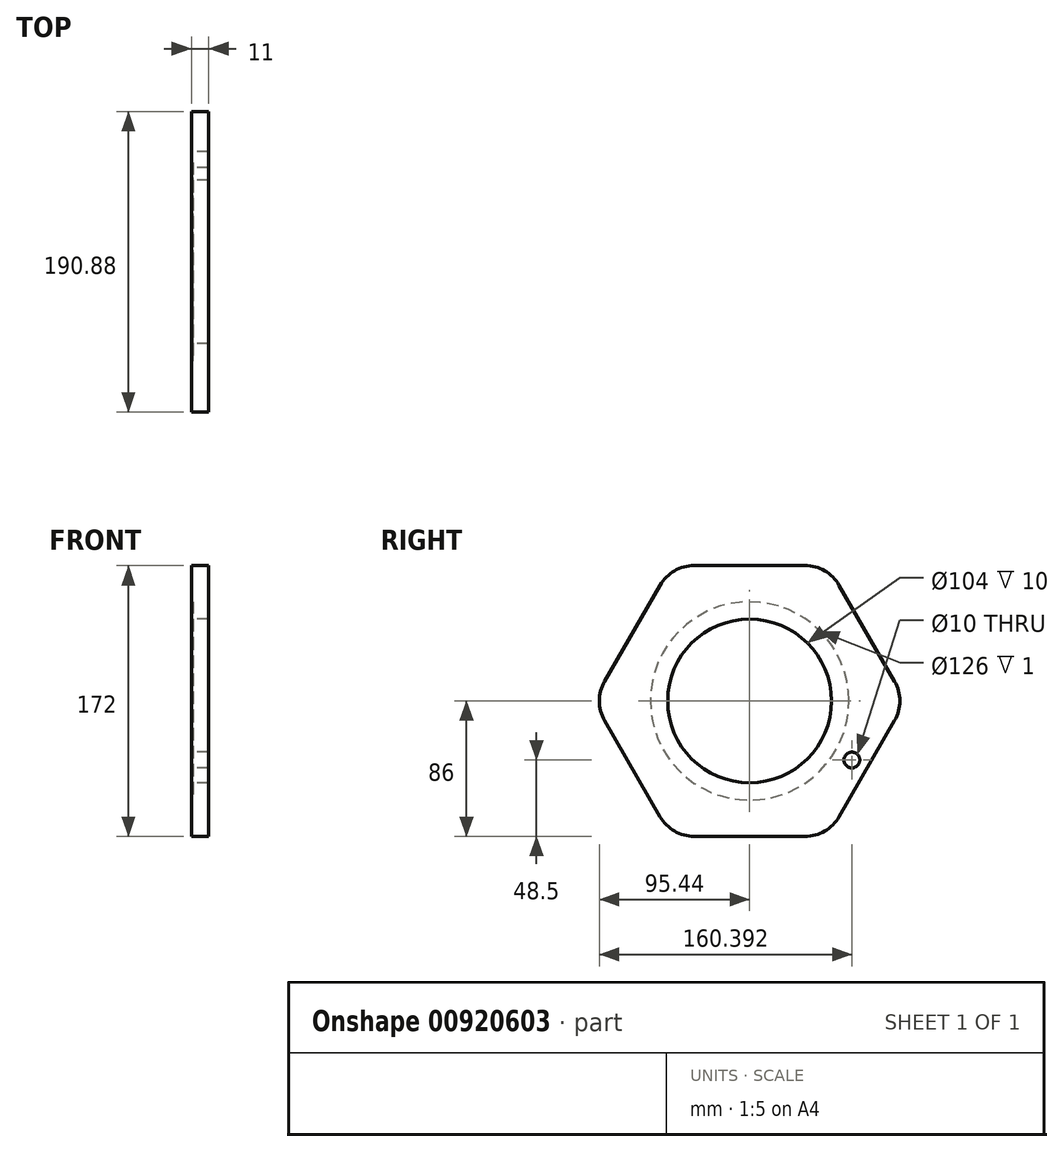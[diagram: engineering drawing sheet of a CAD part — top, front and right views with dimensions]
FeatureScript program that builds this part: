
annotation { "Feature Type Name" : "Feature", "Feature Type Description" : "" }
export const myFeature = defineFeature(function(context is Context, id is Id, definition is map)
    precondition{}
    {
        {
            var Q0;
            Q0=qCreatedBy(makeId("Front.planeOp"),FACE);
            var sketch = newSketch(context, id + "F0", { "sketchPlane" : qUnion([Q0])});
            skLineSegment(sketch, "E0.bottom", {"start": v(67, 35.25) * mm, "end": v(0, 35.25) * mm});
            skLineSegment(sketch, "E0.top", {"start": v(67, 28.15) * mm, "end": v(14, 28.15) * mm});
            skLineSegment(sketch, "E0.left", {"start": v(67, 35.25) * mm, "end": v(67, 28.15) * mm});
            skLineSegment(sketch, "E0.right", {"start": v(0, 35.25) * mm, "end": v(0, 0) * mm});
            skLineSegment(sketch, "E1", {"start": v(14, 0) * mm, "end": v(14, 28.15) * mm});
            skLineSegment(sketch, "E2", {"start": v(14, 0) * mm, "end": v(0, 0) * mm});
            skPoint(sketch, "E3.orphan", {"position": v(26.29, 0) * mm});
            skLineSegment(sketch, "E4", {"start": v(0, 0) * mm, "end": v(-45.98, 0) * mm, "construction": true});
            skSolve(sketch);
        }
        {
            var Q0;
            Q0=makeQuery(id+"F0.imprint","IMPRINT",FACE,{"disambiguationData":[TD([[makeQuery(id+"F0.imprint","IMPRINT",EDGE,{"derivedFrom":sQuery(id+"F0.wireOp",EDGE,"E0.bottom")}),1.0]])]});
            var Q1;
            Q1=sQuery(id+"F0.wireOp",EDGE,"E2");
            revolve(context, id + "F1", {"surfaceOperationType" : NewSurfaceOperationType.NEW, "entities" : qUnion([Q0]), "axis" : qUnion([Q1]), "revolveType" : RevolveType.FULL});
        }
        {
            var Q0;
            Q0=makeQuery(id+"F1.opRevolve","SWEPT_FACE",FACE,{"disambiguationData":[OSD([sQuery(id+"F0.wireOp",EDGE,"E0.right")])]});
            var sketch = newSketch(context, id + "F2", { "sketchPlane" : qUnion([Q0])});
            skCircle(sketch, "E5.cCircle", {"center": v(0, 0) * mm, "radius": 86 * mm, "construction": true});
            skLineSegment(sketch, "E5.0", {"start": v(-49.65, 86) * mm, "end": v(49.65, 86) * mm});
            skLineSegment(sketch, "E5.1", {"start": v(49.65, 86) * mm, "end": v(99.3, 0) * mm});
            skLineSegment(sketch, "E5.2", {"start": v(99.3, 0) * mm, "end": v(49.65, -86) * mm});
            skLineSegment(sketch, "E5.3", {"start": v(49.65, -86) * mm, "end": v(-49.65, -86) * mm});
            skLineSegment(sketch, "E5.4", {"start": v(-49.65, -86) * mm, "end": v(-99.3, 0) * mm});
            skLineSegment(sketch, "E5.5", {"start": v(-99.3, 0) * mm, "end": v(-49.65, 86) * mm});
            skPoint(sketch, "E5.0.midPoint", {"position": v(0, 86) * mm});
            skCircle(sketch, "E6", {"center": v(0, 0) * mm, "radius": 35.25 * mm});
            skSolve(sketch);
        }
        {
            var Q0;
            Q0=makeQuery(id+"F2.imprint","IMPRINT",FACE,{"disambiguationData":[TD([[makeQuery(id+"F2.imprint","IMPRINT",EDGE,{"derivedFrom":sQuery(id+"F2.wireOp",EDGE,"E5.0")}),-1.0]])]});
            extrude(context, id + "F3", {"entities" : qUnion([Q0]), "operationType" : NewBodyOperationType.ADD, "oppositeDirection" : true, "depth" : 11 * mm, "offsetDistance" : 25 * mm});
        }
        {
            var Q0;
            Q0=makeQuery(id+"F3.opExtrude","SWEPT_EDGE",EDGE,{"disambiguationData":[OSD([sQuery(id+"F2.wireOp",EDGE,"E5.3"),sQuery(id+"F2.wireOp",EDGE,"E5.4")])]});
            var Q1;
            Q1=makeQuery(id+"F3.opExtrude","SWEPT_EDGE",EDGE,{"disambiguationData":[OSD([sQuery(id+"F2.wireOp",EDGE,"E5.2"),sQuery(id+"F2.wireOp",EDGE,"E5.3")])]});
            var Q2;
            Q2=makeQuery(id+"F3.opExtrude","SWEPT_EDGE",EDGE,{"disambiguationData":[OSD([sQuery(id+"F2.wireOp",EDGE,"E5.1"),sQuery(id+"F2.wireOp",EDGE,"E5.2")])]});
            var Q3;
            Q3=makeQuery(id+"F3.opExtrude","SWEPT_EDGE",EDGE,{"disambiguationData":[OSD([sQuery(id+"F2.wireOp",EDGE,"E5.0"),sQuery(id+"F2.wireOp",EDGE,"E5.1")])]});
            var Q4;
            Q4=makeQuery(id+"F3.opExtrude","SWEPT_EDGE",EDGE,{"disambiguationData":[OSD([sQuery(id+"F2.wireOp",EDGE,"E5.4"),sQuery(id+"F2.wireOp",EDGE,"E5.5")])]});
            var Q5;
            Q5=makeQuery(id+"F3.opExtrude","SWEPT_EDGE",EDGE,{"disambiguationData":[OSD([sQuery(id+"F2.wireOp",EDGE,"E5.0"),sQuery(id+"F2.wireOp",EDGE,"E5.5")])]});
            fillet(context, id + "F4", {"entities" : qUnion([Q0, Q1, Q2, Q3, Q4, Q5]), "radius" : 25 * mm, "tangentPropagation" : true, "allowEdgeOverflow" : false});
        }
        {
            var Q0;
            Q0=qCreatedBy(makeId("Front.planeOp"),FACE);
            var sketch = newSketch(context, id + "F5", { "sketchPlane" : qUnion([Q0])});
            skLineSegment(sketch, "E7", {"start": v(67, -35.25) * mm, "end": v(11, -35.25) * mm, "construction": true});
            skLineSegment(sketch, "E8.0", {"start": v(11, -12.5) * mm, "end": v(11, -73.5) * mm, "construction": true});
            skLineSegment(sketch, "E9", {"start": v(56, -35.25) * mm, "end": v(11, -35.25) * mm});
            skLineSegment(sketch, "E10", {"start": v(11, -35.25) * mm, "end": v(11, -76) * mm});
            skArc(sketch, "E11", {"start": v(11, -76) * mm, "mid": v(28.9, -67.94) * mm, "end": v(39.73, -51.59) * mm});
            skArc(sketch, "E12", {"start": v(56, -35.25) * mm, "mid": v(45.87, -41.43) * mm, "end": v(39.73, -51.59) * mm});
            skSolve(sketch);
        }
        {
            var Q0;
            Q0=makeQuery(id+"F5.imprint","IMPRINT",FACE,{"disambiguationData":[TD([[makeQuery(id+"F5.imprint","IMPRINT",EDGE,{"derivedFrom":sQuery(id+"F5.wireOp",EDGE,"E9")}),1.0]])]});
            extrude(context, id + "F6", {"entities" : qUnion([Q0]), "operationType" : NewBodyOperationType.ADD, "depth" : 8 * mm, "offsetDistance" : 25 * mm, "hasDraft" : true, "draftAngle" : 3 * degree, "symmetric" : true});
        }
        {
            var Q0;
            Q0=makeQuery(id+"F1.opRevolve","SWEPT_FACE",FACE,{"disambiguationData":[OSD([sQuery(id+"F0.wireOp",EDGE,"E1")])]});
            var sketch = newSketch(context, id + "F7", { "sketchPlane" : qUnion([Q0])});
            skCircle(sketch, "E13", {"center": v(0, 0) * mm, "radius": 17.5 * mm});
            skSolve(sketch);
        }
        {
            var Q0;
            Q0=makeQuery(id+"F7.imprint","IMPRINT",FACE,{"disambiguationData":[TD([[makeQuery(id+"F7.imprint","IMPRINT",EDGE,{"derivedFrom":sQuery(id+"F7.wireOp",EDGE,"E13")}),1.0]])]});
            extrude(context, id + "F8", {"entities" : qUnion([Q0]), "operationType" : NewBodyOperationType.REMOVE, "endBound" : BoundingType.THROUGH_ALL, "oppositeDirection" : true, "depth" : 25 * mm, "offsetDistance" : 25 * mm});
        }
        {
            var Q0;
            Q0=makeQuery(id+"F3.boolean.opBoolean","MERGE",FACE,{"derivedFrom":[makeQuery(id+"F1.opRevolve","SWEPT_FACE",FACE,{"disambiguationData":[OSD([sQuery(id+"F0.wireOp",EDGE,"E0.right")])]}),makeQuery(id+"F3.opExtrude","CAP_FACE",FACE,{"disambiguationData":[OSD([sQuery(id+"F2.wireOp",EDGE,"E5.0"),sQuery(id+"F2.wireOp",EDGE,"E5.1"),sQuery(id+"F2.wireOp",EDGE,"E5.2"),sQuery(id+"F2.wireOp",EDGE,"E5.3"),sQuery(id+"F2.wireOp",EDGE,"E5.4"),sQuery(id+"F2.wireOp",EDGE,"E5.5"),sQuery(id+"F2.wireOp",EDGE,"E6")])],"isStart":true})]});
            var sketch = newSketch(context, id + "F9", { "sketchPlane" : qUnion([Q0])});
            skLineSegment(sketch, "E14", {"start": v(0, 0) * mm, "end": v(-64.95, -37.5) * mm, "construction": true});
            skCircle(sketch, "E15", {"center": v(-64.95, -37.5) * mm, "radius": 5 * mm});
            skSolve(sketch);
        }
        {
            var Q0;
            Q0=makeQuery(id+"F9.imprint","IMPRINT",FACE,{"disambiguationData":[TD([[makeQuery(id+"F9.imprint","IMPRINT",EDGE,{"derivedFrom":sQuery(id+"F9.wireOp",EDGE,"E15")}),1.0]])]});
            extrude(context, id + "F10", {"entities" : qUnion([Q0]), "operationType" : NewBodyOperationType.REMOVE, "endBound" : BoundingType.THROUGH_ALL, "oppositeDirection" : true, "depth" : 25 * mm, "offsetDistance" : 25 * mm});
        }
        {
            var Q0;
            Q0=makeQuery(id+"F3.boolean.opBoolean","MERGE",FACE,{"derivedFrom":[makeQuery(id+"F1.opRevolve","SWEPT_FACE",FACE,{"disambiguationData":[OSD([sQuery(id+"F0.wireOp",EDGE,"E0.right")])]}),makeQuery(id+"F3.opExtrude","CAP_FACE",FACE,{"disambiguationData":[OSD([sQuery(id+"F2.wireOp",EDGE,"E5.0"),sQuery(id+"F2.wireOp",EDGE,"E5.1"),sQuery(id+"F2.wireOp",EDGE,"E5.2"),sQuery(id+"F2.wireOp",EDGE,"E5.3"),sQuery(id+"F2.wireOp",EDGE,"E5.4"),sQuery(id+"F2.wireOp",EDGE,"E5.5"),sQuery(id+"F2.wireOp",EDGE,"E6")])],"isStart":true})]});
            var sketch = newSketch(context, id + "F11", { "sketchPlane" : qUnion([Q0])});
            skCircle(sketch, "E16", {"center": v(0, 0) * mm, "radius": 52 * mm});
            skSolve(sketch);
        }
        {
            var Q0;
            Q0=makeQuery(id+"F11.imprint","IMPRINT",FACE,{"disambiguationData":[TD([[makeQuery(id+"F11.imprint","IMPRINT",EDGE,{"derivedFrom":sQuery(id+"F11.wireOp",EDGE,"E16")}),1.0]])]});
            extrude(context, id + "F12", {"entities" : qUnion([Q0]), "operationType" : NewBodyOperationType.REMOVE, "endBound" : BoundingType.THROUGH_ALL, "oppositeDirection" : true, "depth" : 25 * mm, "offsetDistance" : 25 * mm});
        }
        {
            var Q0;
            Q0=makeQuery(id+"F3.opExtrude","CAP_FACE",FACE,{"disambiguationData":[OSD([sQuery(id+"F2.wireOp",EDGE,"E5.0"),sQuery(id+"F2.wireOp",EDGE,"E5.1"),sQuery(id+"F2.wireOp",EDGE,"E5.2"),sQuery(id+"F2.wireOp",EDGE,"E5.3"),sQuery(id+"F2.wireOp",EDGE,"E5.4"),sQuery(id+"F2.wireOp",EDGE,"E5.5"),sQuery(id+"F2.wireOp",EDGE,"E6")])],"isStart":false});
            var sketch = newSketch(context, id + "F13", { "sketchPlane" : qUnion([Q0])});
            skLineSegment(sketch, "E17.bottom", {"start": v(-125.97, 119.8) * mm, "end": v(142.74, 119.8) * mm});
            skLineSegment(sketch, "E17.top", {"start": v(-125.97, -136.54) * mm, "end": v(142.74, -136.54) * mm});
            skLineSegment(sketch, "E17.left", {"start": v(-125.97, 119.8) * mm, "end": v(-125.97, -136.54) * mm});
            skLineSegment(sketch, "E17.right", {"start": v(142.74, 119.8) * mm, "end": v(142.74, -136.54) * mm});
            skSolve(sketch);
        }
        {
            var Q0;
            Q0=makeQuery(id+"F13.imprint","IMPRINT",FACE,{"disambiguationData":[TD([[makeQuery(id+"F13.imprint","IMPRINT",EDGE,{"derivedFrom":sQuery(id+"F13.wireOp",EDGE,"E17.bottom")}),-1.0]])]});
            var Q1;
            {var subQ9=sQuery(id+"F2.wireOp",EDGE,"E5.0");Q1=makeQuery(id+"F13.imprint","IMPRINT",FACE,{"disambiguationData":[TD([[makeQuery(id+"F13.imprint","IMPRINT",EDGE,{"derivedFrom":makeQuery(id+"F3.opExtrude","CAP_EDGE",EDGE,{"disambiguationData":[OSD([subQ9])],"isStart":false})}),1.0]])]});}
            var Q2;
            {var subQ1=sQuery(id+"F5.wireOp",EDGE,"E11");var subQ4=makeQuery(id+"F3.opExtrude","CAP_FACE",FACE,{"disambiguationData":[OSD([sQuery(id+"F2.wireOp",EDGE,"E5.0"),sQuery(id+"F2.wireOp",EDGE,"E5.1"),sQuery(id+"F2.wireOp",EDGE,"E5.2"),sQuery(id+"F2.wireOp",EDGE,"E5.3"),sQuery(id+"F2.wireOp",EDGE,"E5.4"),sQuery(id+"F2.wireOp",EDGE,"E5.5"),sQuery(id+"F2.wireOp",EDGE,"E6")])],"isStart":false});var subQ8=makeQuery(id+"F6.opExtrude","SWEPT_FACE",FACE,{"disambiguationData":[OSD([subQ1])]});Q2=makeQuery(id+"F13.imprint","IMPRINT",FACE,{"disambiguationData":[TD([[makeQuery(id+"F13.imprint","IMPRINT",EDGE,{"derivedFrom":makeQuery(id+"F6.boolean.opBoolean","INTERSECT",EDGE,{"derivedFrom":[subQ4,makeQuery(id+"F6.*.split.splitOp","SPLIT",FACE,{"derivedFrom":subQ8})]})}),1.0]])]});}
            extrude(context, id + "F14", {"entities" : qUnion([Q0, Q1, Q2]), "operationType" : NewBodyOperationType.REMOVE, "depth" : 40 * mm, "offsetDistance" : 25 * mm});
        }
        {
            var Q0;
            Q0=makeQuery(id+"F3.boolean.opBoolean","MERGE",FACE,{"derivedFrom":[makeQuery(id+"F1.opRevolve","SWEPT_FACE",FACE,{"disambiguationData":[OSD([sQuery(id+"F0.wireOp",EDGE,"E0.right")])]}),makeQuery(id+"F3.opExtrude","CAP_FACE",FACE,{"disambiguationData":[OSD([sQuery(id+"F2.wireOp",EDGE,"E5.0"),sQuery(id+"F2.wireOp",EDGE,"E5.1"),sQuery(id+"F2.wireOp",EDGE,"E5.2"),sQuery(id+"F2.wireOp",EDGE,"E5.3"),sQuery(id+"F2.wireOp",EDGE,"E5.4"),sQuery(id+"F2.wireOp",EDGE,"E5.5"),sQuery(id+"F2.wireOp",EDGE,"E6")])],"isStart":true})]});
            var sketch = newSketch(context, id + "F15", { "sketchPlane" : qUnion([Q0])});
            skCircle(sketch, "E18", {"center": v(0, 0) * mm, "radius": 63 * mm});
            skSolve(sketch);
        }
        {
            var Q0;
            Q0=makeQuery(id+"F15.imprint","IMPRINT",FACE,{"disambiguationData":[TD([[makeQuery(id+"F15.imprint","IMPRINT",EDGE,{"derivedFrom":sQuery(id+"F15.wireOp",EDGE,"E18")}),1.0]])]});
            extrude(context, id + "F16", {"entities" : qUnion([Q0]), "operationType" : NewBodyOperationType.REMOVE, "oppositeDirection" : true, "depth" : 1 * mm, "offsetDistance" : 25 * mm});
        }
    });
